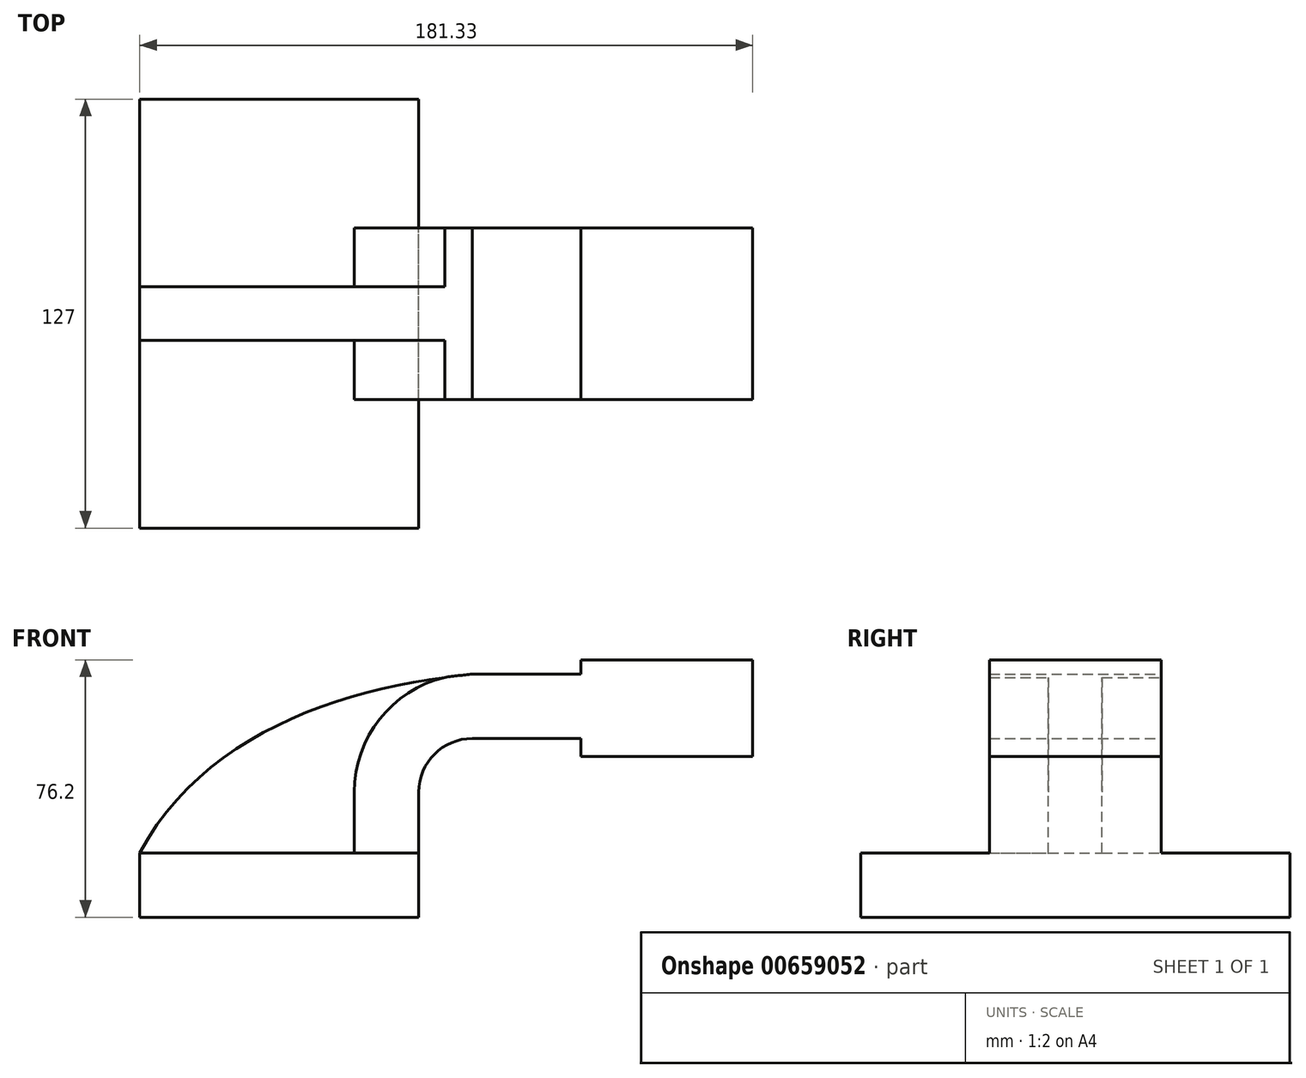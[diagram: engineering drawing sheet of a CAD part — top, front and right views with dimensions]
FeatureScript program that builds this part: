
annotation { "Feature Type Name" : "Feature", "Feature Type Description" : "" }
export const myFeature = defineFeature(function(context is Context, id is Id, definition is map)
    precondition{}
    {
        {
            var Q0;
            Q0=qCreatedBy(makeId("Front.planeOp"),FACE);
            var sketch = newSketch(context, id + "F0", { "sketchPlane" : qUnion([Q0])});
            skLineSegment(sketch, "E0.bottom", {"start": v(41.27, 9.53) * mm, "end": v(-41.27, 9.53) * mm});
            skLineSegment(sketch, "E0.top", {"start": v(41.28, -9.52) * mm, "end": v(-41.27, -9.52) * mm});
            skLineSegment(sketch, "E0.left", {"start": v(41.28, 9.53) * mm, "end": v(41.28, -9.52) * mm});
            skLineSegment(sketch, "E0.right", {"start": v(-41.27, 9.53) * mm, "end": v(-41.27, -9.52) * mm});
            skPoint(sketch, "E0.middle", {"position": v(0, 0) * mm});
            skLineSegment(sketch, "E1.bottom", {"start": v(89.25, 66.68) * mm, "end": v(140.05, 66.68) * mm});
            skLineSegment(sketch, "E1.top", {"start": v(89.25, 38.1) * mm, "end": v(140.05, 38.1) * mm});
            skLineSegment(sketch, "E1.left", {"start": v(89.25, 66.68) * mm, "end": v(89.25, 38.1) * mm});
            skLineSegment(sketch, "E1.right", {"start": v(140.05, 66.68) * mm, "end": v(140.05, 38.1) * mm});
            skPoint(sketch, "E1.middle", {"position": v(114.65, 52.39) * mm});
            skLineSegment(sketch, "E2", {"start": v(41.27, 9.53) * mm, "end": v(41.27, 27.5) * mm});
            skArc(sketch, "E3", {"start": v(41.27, 27.5) * mm, "mid": v(45.92, 38.73) * mm, "end": v(57.15, 43.38) * mm});
            skLineSegment(sketch, "E4", {"start": v(57.15, 43.38) * mm, "end": v(85.72, 43.38) * mm});
            skLineSegment(sketch, "E5.0", {"start": v(57.15, 62.43) * mm, "end": v(113.31, 62.43) * mm});
            skArc(sketch, "E5.1", {"start": v(22.22, 27.5) * mm, "mid": v(32.45, 52.2) * mm, "end": v(57.15, 62.43) * mm});
            skLineSegment(sketch, "E5.2", {"start": v(22.22, 9.53) * mm, "end": v(22.22, 27.5) * mm});
            skLineSegment(sketch, "E6", {"start": v(85.72, 43.38) * mm, "end": v(114.43, 43.38) * mm});
            skLineSegment(sketch, "E7", {"start": v(113.31, 62.43) * mm, "end": v(114.43, 38.1) * mm});
            skFitSpline(sketch, "E8", {"points": [v(-41.27, 9.53) * mm, v(57.15, 62.43) * mm], "startDerivative": vector(58.23, 107.84) * mm, "endDerivative": vector(113.16, 11.37) * mm});
            skSolve(sketch);
        }
        {
            var Q0;
            Q0=makeQuery(id+"F0.imprint","IMPRINT",FACE,{"disambiguationData":[TD([[makeQuery(id+"F0.imprint","IMPRINT",EDGE,{"derivedFrom":sQuery(id+"F0.wireOp",EDGE,"E0.top")}),-1.0]])]});
            extrude(context, id + "F1", {"entities" : qUnion([Q0]), "depth" : 127 * mm, "offsetDistance" : 25.4 * mm, "symmetric" : true});
        }
        {
            var Q0;
            {var subQ0=sQuery(id+"F0.wireOp",EDGE,"E2");Q0=makeQuery(id+"F0.imprint","IMPRINT",FACE,{"disambiguationData":[TD([[makeQuery(id+"F0.imprint","IMPRINT",EDGE,{"derivedFrom":subQ0}),1.0]])]});}
            var Q1;
            {var subQ6=sQuery(id+"F0.wireOp",EDGE,"E1.bottom");Q1=makeQuery(id+"F0.imprint","IMPRINT",FACE,{"disambiguationData":[TD([[makeQuery(id+"F0.imprint","IMPRINT",EDGE,{"derivedFrom":subQ6}),-1.0]])]});}
            var Q2;
            {var subQ0=sQuery(id+"F0.wireOp",EDGE,"E5.0");var subQ1=sQuery(id+"F0.wireOp",EDGE,"E1.left");var subQ2=makeQuery(id+"F0.imprint","INTERSECT",VERTEX,{"derivedFrom":[subQ1,subQ0]});Q2=makeQuery(id+"F0.imprint","IMPRINT",FACE,{"disambiguationData":[TD([[makeQuery(id+"F0.imprint","IMPRINT",EDGE,{"disambiguationData":[TD([[subQ2,-1.0]])],"derivedFrom":subQ1}),1.0]])]});}
            var Q3;
            {var subQ0=sQuery(id+"F0.wireOp",EDGE,"E1.left");var subQ1=sQuery(id+"F0.wireOp",EDGE,"E1.top");var subQ2=makeQuery(id+"F0.imprint","INTERSECT",VERTEX,{"derivedFrom":[subQ1,subQ0]});Q3=makeQuery(id+"F0.imprint","IMPRINT",FACE,{"disambiguationData":[TD([[makeQuery(id+"F0.imprint","IMPRINT",EDGE,{"disambiguationData":[TD([[subQ2,-1.0]])],"derivedFrom":subQ1}),1.0]])]});}
            extrude(context, id + "F2", {"entities" : qUnion([Q0, Q1, Q2, Q3]), "operationType" : NewBodyOperationType.ADD, "depth" : 50.8 * mm, "offsetDistance" : 25.4 * mm, "symmetric" : true});
        }
        {
            var Q0;
            {var subQ3=sQuery(id+"F0.wireOp",EDGE,"E5.2");Q0=makeQuery(id+"F0.imprint","IMPRINT",FACE,{"disambiguationData":[TD([[makeQuery(id+"F0.imprint","IMPRINT",EDGE,{"derivedFrom":subQ3}),1.0]])]});}
            extrude(context, id + "F3", {"entities" : qUnion([Q0]), "operationType" : NewBodyOperationType.ADD, "depth" : 15.88 * mm, "offsetDistance" : 25.4 * mm, "symmetric" : true});
        }
    });
